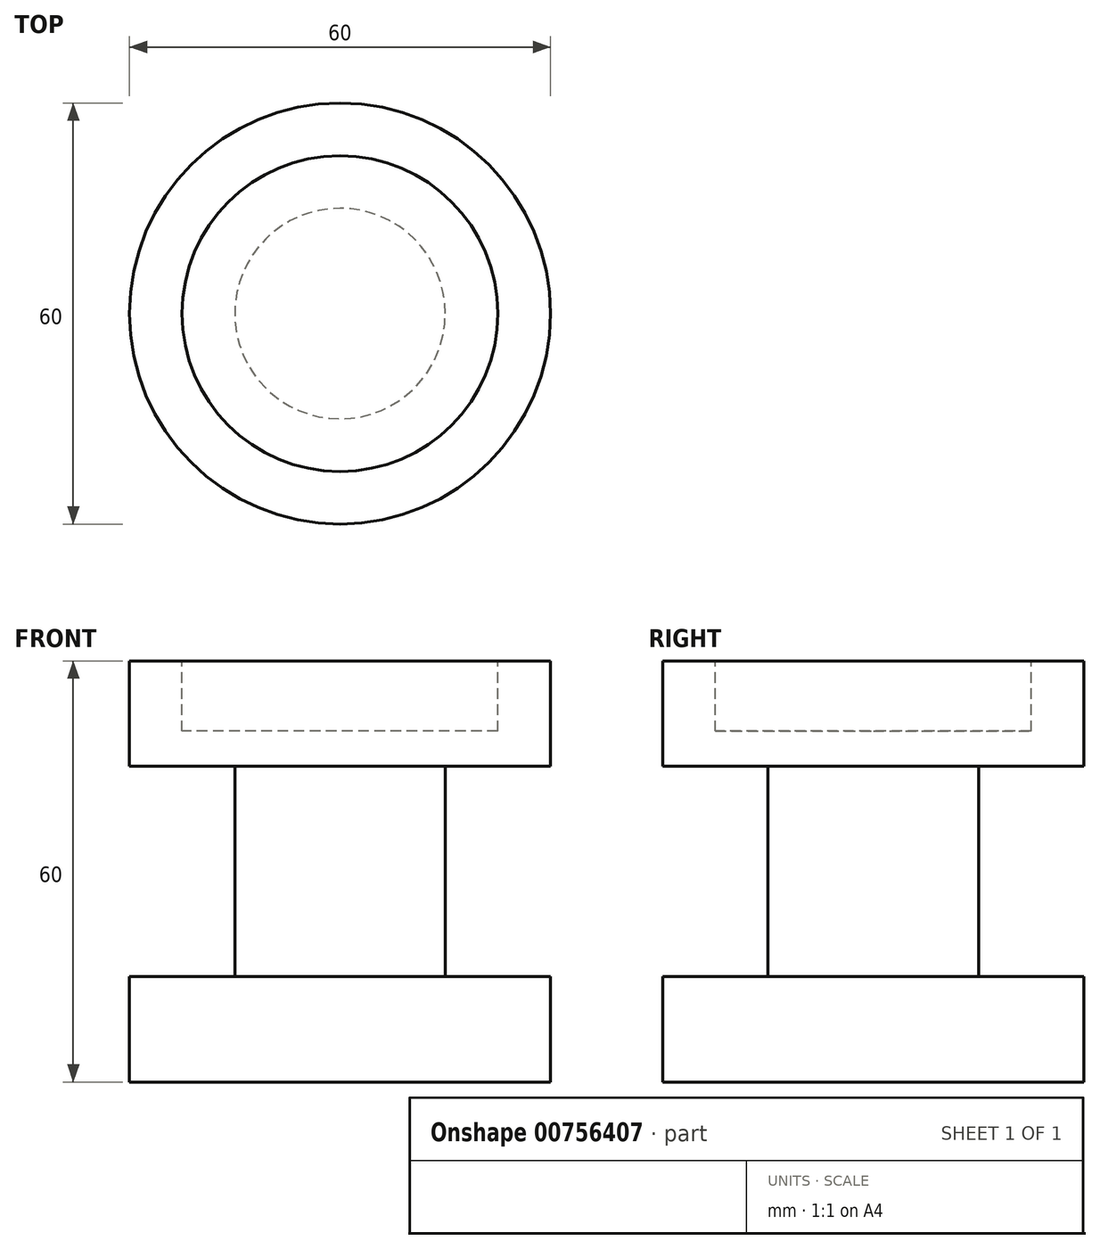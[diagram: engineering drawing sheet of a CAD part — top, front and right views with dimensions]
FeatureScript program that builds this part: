
annotation { "Feature Type Name" : "Feature", "Feature Type Description" : "" }
export const myFeature = defineFeature(function(context is Context, id is Id, definition is map)
    precondition{}
    {
        {
            var Q0;
            Q0=qCreatedBy(makeId("Front.planeOp"),FACE);
            var sketch = newSketch(context, id + "F0", { "sketchPlane" : qUnion([Q0])});
            skLineSegment(sketch, "E0.bottom", {"start": v(0, 0) * mm, "end": v(30, 0) * mm});
            skLineSegment(sketch, "E0.right", {"start": v(30, 0) * mm, "end": v(30, 15) * mm});
            skLineSegment(sketch, "E1.right", {"start": v(15, 15) * mm, "end": v(15, 45) * mm});
            skLineSegment(sketch, "E2.top", {"start": v(0, 60) * mm, "end": v(30, 60) * mm});
            skLineSegment(sketch, "E2.right", {"start": v(30, 45) * mm, "end": v(30, 60) * mm});
            skLineSegment(sketch, "E3", {"start": v(15, 15) * mm, "end": v(30, 15) * mm});
            skLineSegment(sketch, "E4", {"start": v(15, 45) * mm, "end": v(30, 45) * mm});
            skLineSegment(sketch, "E5", {"start": v(0, 60) * mm, "end": v(0, 0) * mm});
            skSolve(sketch);
        }
        {
            var Q0;
            Q0 = qSketchRegion(id + "F0", true);
            var Q1;
            Q1=sQuery(id+"F0.wireOp",EDGE,"E5");
            revolve(context, id + "F1", {"surfaceOperationType" : NewSurfaceOperationType.NEW, "entities" : qUnion([Q0]), "axis" : qUnion([Q1]), "revolveType" : RevolveType.FULL});
        }
        {
            var Q0;
            Q0=makeQuery(id+"F1.opRevolve","SWEPT_FACE",FACE,{"disambiguationData":[OSD([sQuery(id+"F0.wireOp",EDGE,"E2.top")])]});
            var sketch = newSketch(context, id + "F2", { "sketchPlane" : qUnion([Q0])});
            skCircle(sketch, "E6", {"center": v(0, 0) * mm, "radius": 22.5 * mm});
            skSolve(sketch);
        }
        {
            var Q0;
            Q0 = qSketchRegion(id + "F2", true);
            extrude(context, id + "F3", {"entities" : qUnion([Q0]), "operationType" : NewBodyOperationType.REMOVE, "oppositeDirection" : true, "depth" : 10 * mm, "offsetDistance" : 25 * mm});
        }
    });
